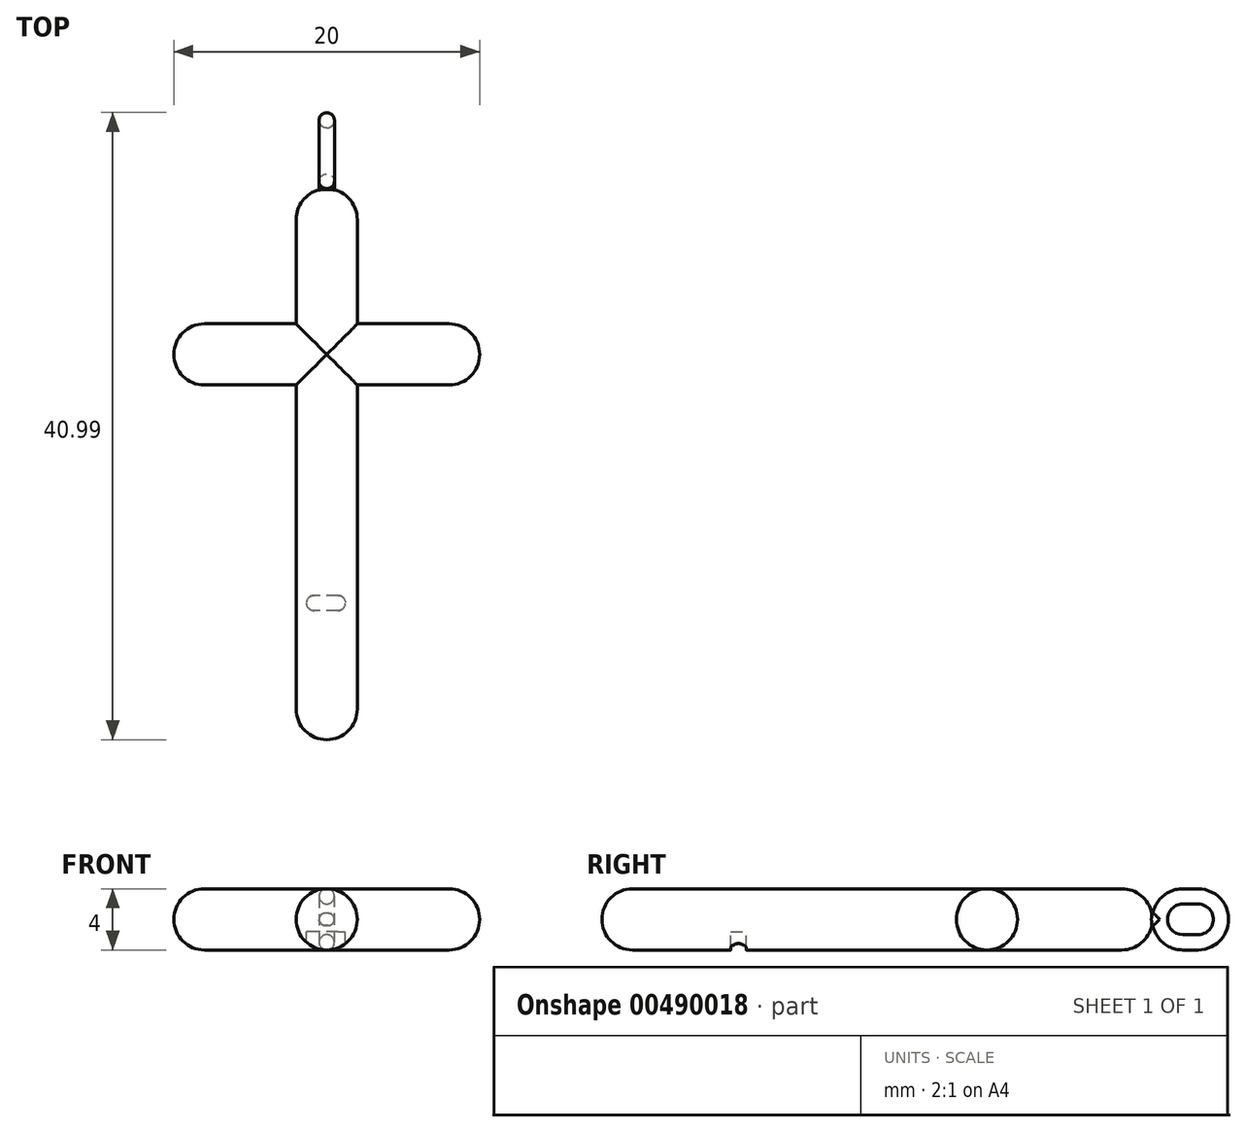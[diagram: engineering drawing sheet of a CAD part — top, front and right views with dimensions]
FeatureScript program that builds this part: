
annotation { "Feature Type Name" : "Feature", "Feature Type Description" : "" }
export const myFeature = defineFeature(function(context is Context, id is Id, definition is map)
    precondition{}
    {
        {
            var Q0;
            Q0=qCreatedBy(makeId("Top.planeOp"),FACE);
            var sketch = newSketch(context, id + "F0", { "sketchPlane" : qUnion([Q0])});
            skLineSegment(sketch, "E0.bottom", {"start": v(2, -18) * mm, "end": v(-2, -18) * mm});
            skLineSegment(sketch, "E0.top", {"start": v(2, 18) * mm, "end": v(-2, 18) * mm});
            skLineSegment(sketch, "E0.left", {"start": v(2, -18) * mm, "end": v(2, 18) * mm});
            skLineSegment(sketch, "E0.right", {"start": v(-2, -18) * mm, "end": v(-2, 18) * mm});
            skPoint(sketch, "E0.middle", {"position": v(0, 0) * mm});
            skLineSegment(sketch, "E1.bottom", {"start": v(10, 9.18) * mm, "end": v(-10, 9.18) * mm});
            skLineSegment(sketch, "E1.top", {"start": v(10, 5.18) * mm, "end": v(-10, 5.18) * mm});
            skLineSegment(sketch, "E1.left", {"start": v(10, 9.18) * mm, "end": v(10, 5.18) * mm});
            skLineSegment(sketch, "E1.right", {"start": v(-10, 9.18) * mm, "end": v(-10, 5.18) * mm});
            skPoint(sketch, "E1.middle", {"position": v(0, 7.18) * mm});
            skSolve(sketch);
        }
        {
            var Q0;
            {var subQ5=sQuery(id+"F0.wireOp",EDGE,"E1.left");Q0=makeQuery(id+"F0.imprint","IMPRINT",FACE,{"disambiguationData":[TD([[makeQuery(id+"F0.imprint","IMPRINT",EDGE,{"derivedFrom":subQ5}),-1.0]])]});}
            var Q1;
            {var subQ0=sQuery(id+"F0.wireOp",EDGE,"E1.top");var subQ1=sQuery(id+"F0.wireOp",EDGE,"E0.left");var subQ2=makeQuery(id+"F0.imprint","INTERSECT",VERTEX,{"derivedFrom":[subQ1,subQ0]});Q1=makeQuery(id+"F0.imprint","IMPRINT",FACE,{"disambiguationData":[TD([[makeQuery(id+"F0.imprint","IMPRINT",EDGE,{"disambiguationData":[TD([[subQ2,-1.0]])],"derivedFrom":subQ1}),1.0]])]});}
            var Q2;
            {var subQ0=sQuery(id+"F0.wireOp",EDGE,"E0.top");Q2=makeQuery(id+"F0.imprint","IMPRINT",FACE,{"disambiguationData":[TD([[makeQuery(id+"F0.imprint","IMPRINT",EDGE,{"derivedFrom":subQ0}),1.0]])]});}
            var Q3;
            {var subQ5=sQuery(id+"F0.wireOp",EDGE,"E1.right");Q3=makeQuery(id+"F0.imprint","IMPRINT",FACE,{"disambiguationData":[TD([[makeQuery(id+"F0.imprint","IMPRINT",EDGE,{"derivedFrom":subQ5}),1.0]])]});}
            var Q4;
            {var subQ0=sQuery(id+"F0.wireOp",EDGE,"E0.bottom");Q4=makeQuery(id+"F0.imprint","IMPRINT",FACE,{"disambiguationData":[TD([[makeQuery(id+"F0.imprint","IMPRINT",EDGE,{"derivedFrom":subQ0}),-1.0]])]});}
            extrude(context, id + "F1", {"entities" : qUnion([Q0, Q1, Q2, Q3, Q4]), "depth" : 2 * mm, "offsetDistance" : 25 * mm, "hasSecondDirection" : true, "secondDirectionOppositeDirection" : true, "secondDirectionDepth" : 2 * mm});
        }
        {
            var Q0;
            Q0=makeQuery(id+"F1.opExtrude","SWEPT_EDGE",EDGE,{"disambiguationData":[OSD([sQuery(id+"F0.wireOp",EDGE,"E0.bottom"),sQuery(id+"F0.wireOp",EDGE,"E0.left")])]});
            var Q1;
            Q1=makeQuery(id+"F1.opExtrude","SWEPT_EDGE",EDGE,{"disambiguationData":[OSD([sQuery(id+"F0.wireOp",EDGE,"E0.bottom"),sQuery(id+"F0.wireOp",EDGE,"E0.right")])]});
            var Q2;
            Q2=makeQuery(id+"F1.opExtrude","SWEPT_EDGE",EDGE,{"disambiguationData":[OSD([sQuery(id+"F0.wireOp",EDGE,"E1.top"),sQuery(id+"F0.wireOp",EDGE,"E1.right")])]});
            var Q3;
            Q3=makeQuery(id+"F1.opExtrude","SWEPT_EDGE",EDGE,{"disambiguationData":[OSD([sQuery(id+"F0.wireOp",EDGE,"E1.bottom"),sQuery(id+"F0.wireOp",EDGE,"E1.right")])]});
            var Q4;
            Q4=makeQuery(id+"F1.opExtrude","SWEPT_EDGE",EDGE,{"disambiguationData":[OSD([sQuery(id+"F0.wireOp",EDGE,"E1.top"),sQuery(id+"F0.wireOp",EDGE,"E1.left")])]});
            var Q5;
            Q5=makeQuery(id+"F1.opExtrude","SWEPT_EDGE",EDGE,{"disambiguationData":[OSD([sQuery(id+"F0.wireOp",EDGE,"E1.bottom"),sQuery(id+"F0.wireOp",EDGE,"E1.left")])]});
            var Q6;
            Q6=makeQuery(id+"F1.opExtrude","SWEPT_EDGE",EDGE,{"disambiguationData":[OSD([sQuery(id+"F0.wireOp",EDGE,"E0.top"),sQuery(id+"F0.wireOp",EDGE,"E0.left")])]});
            var Q7;
            Q7=makeQuery(id+"F1.opExtrude","SWEPT_EDGE",EDGE,{"disambiguationData":[OSD([sQuery(id+"F0.wireOp",EDGE,"E0.top"),sQuery(id+"F0.wireOp",EDGE,"E0.right")])]});
            fillet(context, id + "F2", {"entities" : qUnion([Q0, Q1, Q2, Q3, Q4, Q5, Q6, Q7]), "radius" : 2 * mm, "tangentPropagation" : true, "allowEdgeOverflow" : false});
        }
        {
            var Q0;
            {var subQ0=sQuery(id+"F0.wireOp",EDGE,"E0.left");Q0=makeQuery(id+"F1.opExtrude","CAP_EDGE",EDGE,{"disambiguationData":[OSD([subQ0]),TDD([makeQuery(id+"F0.imprint","IMPRINT",EDGE,{"disambiguationData":[TD([[makeQuery(id+"F0.imprint","INTERSECT",VERTEX,{"derivedFrom":[sQuery(id+"F0.wireOp",EDGE,"E0.bottom"),subQ0]}),-1.0]])],"derivedFrom":subQ0})])],"isStart":false});}
            var Q1;
            {var subQ0=sQuery(id+"F0.wireOp",EDGE,"E0.right");Q1=makeQuery(id+"F1.opExtrude","CAP_EDGE",EDGE,{"disambiguationData":[OSD([subQ0]),TDD([makeQuery(id+"F0.imprint","IMPRINT",EDGE,{"disambiguationData":[TD([[makeQuery(id+"F0.imprint","INTERSECT",VERTEX,{"derivedFrom":[sQuery(id+"F0.wireOp",EDGE,"E0.bottom"),subQ0]}),-1.0]])],"derivedFrom":subQ0})])],"isStart":false});}
            var Q2;
            {var subQ0=sQuery(id+"F0.wireOp",EDGE,"E1.bottom");Q2=makeQuery(id+"F1.opExtrude","CAP_EDGE",EDGE,{"disambiguationData":[OSD([subQ0]),TDD([makeQuery(id+"F0.imprint","IMPRINT",EDGE,{"disambiguationData":[TD([[makeQuery(id+"F0.imprint","INTERSECT",VERTEX,{"derivedFrom":[subQ0,sQuery(id+"F0.wireOp",EDGE,"E1.left")]}),-1.0]])],"derivedFrom":subQ0})])],"isStart":false});}
            var Q3;
            {var subQ0=sQuery(id+"F0.wireOp",EDGE,"E0.right");Q3=makeQuery(id+"F1.opExtrude","CAP_EDGE",EDGE,{"disambiguationData":[OSD([subQ0]),TDD([makeQuery(id+"F0.imprint","IMPRINT",EDGE,{"disambiguationData":[TD([[makeQuery(id+"F0.imprint","INTERSECT",VERTEX,{"derivedFrom":[sQuery(id+"F0.wireOp",EDGE,"E0.top"),subQ0]}),1.0]])],"derivedFrom":subQ0})])],"isStart":false});}
            var Q4;
            {var subQ0=sQuery(id+"F0.wireOp",EDGE,"E1.bottom");Q4=makeQuery(id+"F1.opExtrude","CAP_EDGE",EDGE,{"disambiguationData":[OSD([subQ0]),TDD([makeQuery(id+"F0.imprint","IMPRINT",EDGE,{"disambiguationData":[TD([[makeQuery(id+"F0.imprint","INTERSECT",VERTEX,{"derivedFrom":[subQ0,sQuery(id+"F0.wireOp",EDGE,"E1.right")]}),1.0]])],"derivedFrom":subQ0})])],"isStart":false});}
            var Q5;
            {var subQ0=sQuery(id+"F0.wireOp",EDGE,"E1.top");Q5=makeQuery(id+"F1.opExtrude","CAP_EDGE",EDGE,{"disambiguationData":[OSD([subQ0]),TDD([makeQuery(id+"F0.imprint","IMPRINT",EDGE,{"disambiguationData":[TD([[makeQuery(id+"F0.imprint","INTERSECT",VERTEX,{"derivedFrom":[subQ0,sQuery(id+"F0.wireOp",EDGE,"E1.right")]}),1.0]])],"derivedFrom":subQ0})])],"isStart":false});}
            var Q6;
            {var subQ0=sQuery(id+"F0.wireOp",EDGE,"E1.top");Q6=makeQuery(id+"F1.opExtrude","CAP_EDGE",EDGE,{"disambiguationData":[OSD([subQ0]),TDD([makeQuery(id+"F0.imprint","IMPRINT",EDGE,{"disambiguationData":[TD([[makeQuery(id+"F0.imprint","INTERSECT",VERTEX,{"derivedFrom":[subQ0,sQuery(id+"F0.wireOp",EDGE,"E1.left")]}),-1.0]])],"derivedFrom":subQ0})])],"isStart":false});}
            var Q7;
            {var subQ0=sQuery(id+"F0.wireOp",EDGE,"E0.left");Q7=makeQuery(id+"F1.opExtrude","CAP_EDGE",EDGE,{"disambiguationData":[OSD([subQ0]),TDD([makeQuery(id+"F0.imprint","IMPRINT",EDGE,{"disambiguationData":[TD([[makeQuery(id+"F0.imprint","INTERSECT",VERTEX,{"derivedFrom":[sQuery(id+"F0.wireOp",EDGE,"E0.top"),subQ0]}),1.0]])],"derivedFrom":subQ0})])],"isStart":true});}
            var Q8;
            {var subQ0=sQuery(id+"F0.wireOp",EDGE,"E1.bottom");Q8=makeQuery(id+"F1.opExtrude","CAP_EDGE",EDGE,{"disambiguationData":[OSD([subQ0]),TDD([makeQuery(id+"F0.imprint","IMPRINT",EDGE,{"disambiguationData":[TD([[makeQuery(id+"F0.imprint","INTERSECT",VERTEX,{"derivedFrom":[subQ0,sQuery(id+"F0.wireOp",EDGE,"E1.left")]}),-1.0]])],"derivedFrom":subQ0})])],"isStart":true});}
            var Q9;
            {var subQ0=sQuery(id+"F0.wireOp",EDGE,"E1.bottom");Q9=makeQuery(id+"F1.opExtrude","CAP_EDGE",EDGE,{"disambiguationData":[OSD([subQ0]),TDD([makeQuery(id+"F0.imprint","IMPRINT",EDGE,{"disambiguationData":[TD([[makeQuery(id+"F0.imprint","INTERSECT",VERTEX,{"derivedFrom":[subQ0,sQuery(id+"F0.wireOp",EDGE,"E1.right")]}),1.0]])],"derivedFrom":subQ0})])],"isStart":true});}
            var Q10;
            {var subQ0=sQuery(id+"F0.wireOp",EDGE,"E0.right");Q10=makeQuery(id+"F1.opExtrude","CAP_EDGE",EDGE,{"disambiguationData":[OSD([subQ0]),TDD([makeQuery(id+"F0.imprint","IMPRINT",EDGE,{"disambiguationData":[TD([[makeQuery(id+"F0.imprint","INTERSECT",VERTEX,{"derivedFrom":[sQuery(id+"F0.wireOp",EDGE,"E0.bottom"),subQ0]}),-1.0]])],"derivedFrom":subQ0})])],"isStart":true});}
            fillet(context, id + "F3", {"entities" : qUnion([Q0, Q1, Q2, Q3, Q4, Q5, Q6, Q7, Q8, Q9, Q10]), "radius" : 2 * mm, "tangentPropagation" : true, "allowEdgeOverflow" : false});
        }
        {
            var Q0;
            Q0=qCreatedBy(makeId("Right.planeOp"),FACE);
            var sketch = newSketch(context, id + "F4", { "sketchPlane" : qUnion([Q0])});
            skLineSegment(sketch, "E2.bottom", {"start": v(19.99, -1) * mm, "end": v(20.99, -1) * mm});
            skLineSegment(sketch, "E2.top", {"start": v(19.99, 1) * mm, "end": v(20.99, 1) * mm});
            skLineSegment(sketch, "E2.left", {"start": v(18.99, 0) * mm, "end": v(18.99, 0) * mm});
            skLineSegment(sketch, "E2.right", {"start": v(21.99, 0) * mm, "end": v(21.99, 0) * mm});
            skPoint(sketch, "E2.middle", {"position": v(20.49, 0) * mm});
            skLineSegment(sketch, "E3.0", {"start": v(22.99, 0) * mm, "end": v(22.99, 0) * mm});
            skLineSegment(sketch, "E3.1", {"start": v(19.99, -2) * mm, "end": v(20.99, -2) * mm});
            skLineSegment(sketch, "E3.2", {"start": v(17.99, 0) * mm, "end": v(17.99, 0) * mm});
            skLineSegment(sketch, "E3.3", {"start": v(19.99, 2) * mm, "end": v(20.99, 2) * mm});
            skPoint(sketch, "E4.visualSharp", {"position": v(21.99, -1) * mm});
            skArc(sketch, "E4.filletArc", {"start": v(20.99, -1) * mm, "mid": v(21.7, -0.7) * mm, "end": v(21.99, 0) * mm});
            skPoint(sketch, "E5.visualSharp", {"position": v(18.99, -1) * mm});
            skArc(sketch, "E5.filletArc", {"start": v(18.99, 0) * mm, "mid": v(19.28, -0.7) * mm, "end": v(19.99, -1) * mm});
            skPoint(sketch, "E6.visualSharp", {"position": v(18.99, 1) * mm});
            skArc(sketch, "E6.filletArc", {"start": v(19.99, 1) * mm, "mid": v(19.28, 0.7) * mm, "end": v(18.99, 0) * mm});
            skPoint(sketch, "E7.visualSharp", {"position": v(21.99, 1) * mm});
            skArc(sketch, "E7.filletArc", {"start": v(21.99, 0) * mm, "mid": v(21.7, 0.7) * mm, "end": v(20.99, 1) * mm});
            skPoint(sketch, "E8.visualSharp", {"position": v(22.99, -2) * mm});
            skArc(sketch, "E8.filletArc", {"start": v(20.99, -2) * mm, "mid": v(22.4, -1.41) * mm, "end": v(22.99, 0) * mm});
            skPoint(sketch, "E9.visualSharp", {"position": v(17.99, -2) * mm});
            skArc(sketch, "E9.filletArc", {"start": v(17.99, 0) * mm, "mid": v(18.57, -1.41) * mm, "end": v(19.99, -2) * mm});
            skPoint(sketch, "E10.visualSharp", {"position": v(17.99, 2) * mm});
            skArc(sketch, "E10.filletArc", {"start": v(19.99, 2) * mm, "mid": v(18.57, 1.41) * mm, "end": v(17.99, 0) * mm});
            skPoint(sketch, "E11.visualSharp", {"position": v(22.99, 2) * mm});
            skArc(sketch, "E11.filletArc", {"start": v(22.99, 0) * mm, "mid": v(22.4, 1.41) * mm, "end": v(20.99, 2) * mm});
            skLineSegment(sketch, "E12.bottom", {"start": v(17.71, -0.4) * mm, "end": v(18.37, -0.4) * mm});
            skLineSegment(sketch, "E12.top", {"start": v(17.71, 0.4) * mm, "end": v(18.37, 0.4) * mm});
            skLineSegment(sketch, "E12.left", {"start": v(17.71, -0.4) * mm, "end": v(17.71, 0.4) * mm});
            skLineSegment(sketch, "E12.right", {"start": v(18.37, -0.4) * mm, "end": v(18.37, 0.4) * mm});
            skPoint(sketch, "E12.middle", {"position": v(18.04, 0) * mm});
            skSolve(sketch);
        }
        {
            var Q0;
            Q0=makeQuery(id+"F4.imprint","IMPRINT",FACE,{"disambiguationData":[TD([[makeQuery(id+"F4.imprint","IMPRINT",EDGE,{"derivedFrom":sQuery(id+"F4.wireOp",EDGE,"E2.bottom")}),-1.0]])]});
            var Q1;
            {var subQ0=sQuery(id+"F4.wireOp",EDGE,"E12.right");Q1=makeQuery(id+"F4.imprint","IMPRINT",FACE,{"disambiguationData":[TD([[makeQuery(id+"F4.imprint","IMPRINT",EDGE,{"derivedFrom":subQ0}),1.0]])]});}
            var Q2;
            {var subQ0=sQuery(id+"F4.wireOp",EDGE,"E12.left");Q2=makeQuery(id+"F4.imprint","IMPRINT",FACE,{"disambiguationData":[TD([[makeQuery(id+"F4.imprint","IMPRINT",EDGE,{"derivedFrom":subQ0}),-1.0]])]});}
            extrude(context, id + "F5", {"entities" : qUnion([Q0, Q1, Q2]), "operationType" : NewBodyOperationType.ADD, "depth" : .5 * mm, "offsetDistance" : 25 * mm, "hasSecondDirection" : true, "secondDirectionOppositeDirection" : true, "secondDirectionDepth" : .5 * mm});
        }
        {
            var Q0;
            Q0=makeQuery(id+"F5.opExtrude","CAP_EDGE",EDGE,{"disambiguationData":[OSD([sQuery(id+"F4.wireOp",EDGE,"E2.top")])],"isStart":false});
            var Q1;
            Q1=makeQuery(id+"F5.opExtrude","CAP_EDGE",EDGE,{"disambiguationData":[OSD([sQuery(id+"F4.wireOp",EDGE,"E8.filletArc"),sQuery(id+"F4.wireOp",EDGE,"E11.filletArc")])],"isStart":false});
            var Q2;
            Q2=makeQuery(id+"F5.opExtrude","CAP_EDGE",EDGE,{"disambiguationData":[OSD([sQuery(id+"F4.wireOp",EDGE,"E8.filletArc"),sQuery(id+"F4.wireOp",EDGE,"E11.filletArc")])],"isStart":true});
            var Q3;
            Q3=makeQuery(id+"F5.opExtrude","CAP_EDGE",EDGE,{"disambiguationData":[OSD([sQuery(id+"F4.wireOp",EDGE,"E5.filletArc"),sQuery(id+"F4.wireOp",EDGE,"E6.filletArc")])],"isStart":true});
            fillet(context, id + "F6", {"entities" : qUnion([Q0, Q1, Q2, Q3]), "radius" : .5 * mm, "tangentPropagation" : true, "allowEdgeOverflow" : false});
        }
        {
            var Q0;
            Q0=makeQuery(id+"F5.opExtrude","CAP_EDGE",EDGE,{"disambiguationData":[OSD([sQuery(id+"F4.wireOp",EDGE,"E12.bottom")])],"isStart":true});
            var Q1;
            Q1=makeQuery(id+"F5.opExtrude","CAP_EDGE",EDGE,{"disambiguationData":[OSD([sQuery(id+"F4.wireOp",EDGE,"E12.top")])],"isStart":true});
            var Q2;
            Q2=makeQuery(id+"F5.opExtrude","CAP_EDGE",EDGE,{"disambiguationData":[OSD([sQuery(id+"F4.wireOp",EDGE,"E12.bottom")])],"isStart":false});
            var Q3;
            Q3=makeQuery(id+"F5.opExtrude","CAP_EDGE",EDGE,{"disambiguationData":[OSD([sQuery(id+"F4.wireOp",EDGE,"E12.top")])],"isStart":false});
            fillet(context, id + "F7", {"entities" : qUnion([Q0, Q1, Q2, Q3]), "radius" : .4 * mm, "tangentPropagation" : true, "allowEdgeOverflow" : false});
        }
        {
            var Q0;
            Q0=qCreatedBy(makeId("Top.planeOp"),FACE);
            var sketch = newSketch(context, id + "F8", { "sketchPlane" : qUnion([Q0])});
            skLineSegment(sketch, "E13.bottom", {"start": v(1.23, -10.37) * mm, "end": v(-0.27, -10.37) * mm});
            skArc(sketch, "E14.filletArc", {"start": v(1.73, -10.87) * mm, "mid": v(1.58, -10.52) * mm, "end": v(1.23, -10.37) * mm});
            skArc(sketch, "E15.filletArc", {"start": v(-0.77, -10.87) * mm, "mid": v(-0.63, -11.22) * mm, "end": v(-0.27, -11.37) * mm});
            skArc(sketch, "E16.filletArc", {"start": v(-0.27, -10.37) * mm, "mid": v(-0.62, -10.52) * mm, "end": v(-0.77, -10.87) * mm});
            skLineSegment(sketch, "E17.bottom", {"start": v(0.73, -8.57) * mm, "end": v(-0.82, -8.57) * mm});
            skLineSegment(sketch, "E17.top", {"start": v(0.73, -9.57) * mm, "end": v(-0.82, -9.57) * mm});
            skArc(sketch, "E18.filletArc", {"start": v(0.73, -9.57) * mm, "mid": v(1, -9.49) * mm, "end": v(1.19, -9.27) * mm});
            skArc(sketch, "E19.filletArc", {"start": v(1.19, -9.27) * mm, "mid": v(1.14, -8.8) * mm, "end": v(0.73, -8.57) * mm});
            skArc(sketch, "E20.filletArc", {"start": v(-1.31, -9.14) * mm, "mid": v(-1.15, -9.45) * mm, "end": v(-0.82, -9.57) * mm});
            skArc(sketch, "E21.filletArc", {"start": v(-0.82, -8.57) * mm, "mid": v(-1.2, -8.74) * mm, "end": v(-1.31, -9.14) * mm});
            skCircle(sketch, "E22", {"center": v(0, -10.86) * mm, "radius": 0.4 * mm});
            skLineSegment(sketch, "E23.bottom", {"start": v(1.07, -12.22) * mm, "end": v(-1.02, -12.22) * mm});
            skLineSegment(sketch, "E23.top", {"start": v(0.48, -13.22) * mm, "end": v(-1.02, -13.22) * mm});
            skArc(sketch, "E24.filletArc", {"start": v(0.48, -13.22) * mm, "mid": v(0.83, -13.07) * mm, "end": v(0.98, -12.72) * mm});
            skArc(sketch, "E25.filletArc", {"start": v(1.57, -12.72) * mm, "mid": v(1.42, -12.37) * mm, "end": v(1.07, -12.22) * mm});
            skArc(sketch, "E26.filletArc", {"start": v(-1.52, -12.72) * mm, "mid": v(-1.38, -13.07) * mm, "end": v(-1.02, -13.22) * mm});
            skArc(sketch, "E27.filletArc", {"start": v(-1.02, -12.22) * mm, "mid": v(-1.38, -12.37) * mm, "end": v(-1.52, -12.72) * mm});
            skSolve(sketch);
        }
        {
            var Q0;
            Q0=makeQuery(id+"F8.imprint","IMPRINT",FACE,{"disambiguationData":[TD([[makeQuery(id+"F8.imprint","IMPRINT",EDGE,{"derivedFrom":sQuery(id+"F8.wireOp",EDGE,"E17.bottom")}),1.0]])]});
            var Q1;
            Q1=makeQuery(id+"F8.imprint","IMPRINT",FACE,{"disambiguationData":[TD([[makeQuery(id+"F8.imprint","IMPRINT",EDGE,{"derivedFrom":sQuery(id+"F8.wireOp",EDGE,"E13.bottom")}),1.0]])]});
            var Q2;
            Q2=makeQuery(id+"F8.imprint","IMPRINT",FACE,{"disambiguationData":[TD([[makeQuery(id+"F8.imprint","IMPRINT",EDGE,{"derivedFrom":sQuery(id+"F8.wireOp",EDGE,"E23.bottom")}),1.0]])]});
            extrude(context, id + "F9", {"entities" : qUnion([Q0, Q1, Q2]), "operationType" : NewBodyOperationType.REMOVE, "oppositeDirection" : true, "depth" : 25 * mm, "offsetDistance" : 25 * mm, "hasSecondDirection" : true, "secondDirectionOppositeDirection" : true, "secondDirectionDepth" : .8 * mm});
        }
    });
